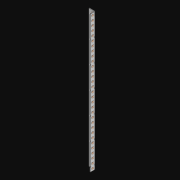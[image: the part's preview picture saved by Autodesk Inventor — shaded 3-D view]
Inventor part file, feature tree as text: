
AUTODESK INVENTOR PART (.ipt)
format: ipt  version: 2021 (Build 250183000, 183)  size: 1,305,600 bytes
history: native  units: in
note: dims shown in document units (in); Inventor stores cm internally (conversion verified against a paired STEP export)
features: extrude x64, other x62, sketch x4, pattern_linear x2, sheet_metal_op x1
ambient origin geometry x8: Origin, YZ Plane, XZ Plane, XY Plane, X Axis, Y Axis, Z Axis, Center Point
bodies: Solid1 (feature_tree)
feature tree (133):
  pattern_linear  "Rectangular Pattern1"  Spacing1=0.5in  [1 undecoded]
  pattern_linear  "Rectangular Pattern3"  Count1=31  [1 undecoded]
  extrude  "Extrusion1"  Depth=0.5in
  extrude  "Extrusion2"  Depth=0.5in
  sketch  "Sketch1"  dims[d0=0.182in]
  other  "Srf1"
  sketch  "Sketch3"  dims[d1=0.063in d2=0.0in]
  other  "Srf3"
  other  "Srf4"
  other  "Srf5"
  other  "Srf6"
  other  "Srf7"
  other  "Srf8"
  other  "Srf9"
  other  "Srf10"
  other  "Srf11"
  other  "Srf12"
  other  "Srf13"
  other  "Srf14"
  other  "Srf15"
  other  "Srf16"
  other  "Srf17"
  other  "Srf18"
  other  "Srf19"
  other  "Srf20"
  other  "Srf21"
  other  "Srf22"
  other  "Srf23"
  other  "Srf24"
  other  "Srf25"
  other  "Srf26"
  other  "Srf27"
  other  "Srf28"
  other  "Srf29"
  other  "Srf30"
  other  "Srf31"
  other  "Srf32"
  other  "Srf33"
  other  "Srf142"
  other  "Srf143"
  other  "Srf144"
  other  "Srf145"
  other  "Srf146"
  other  "Srf147"
  other  "Srf148"
  other  "Srf149"
  other  "Srf150"
  other  "Srf151"
  other  "Srf152"
  other  "Srf153"
  other  "Srf154"
  other  "Srf155"
  other  "Srf156"
  other  "Srf157"
  other  "Srf158"
  other  "Srf159"
  other  "Srf160"
  other  "Srf161"
  other  "Srf162"
  other  "Srf163"
  other  "Srf164"
  other  "Srf165"
  other  "Srf166"
  other  "Srf167"
  other  "Srf168"
  other  "Srf169"
  other  "Srf170"
  other  "Srf171"
  sketch  "Sketch4"  dims[d6=0.182in]
  sketch  "Sketch5"  dims[d7=0.063in d8=0.0in d11=0.5in d12=0.3937in d14=0.5in d18=12.2047in d20=0.5in d21=2.0in d22=0.0in d23=0.841in d24=0.0in]
  sheet_metal_op  "Fold1"
  extrude  "ExtrusionSrf1"  TaperAngle=0.0deg  [1 undecoded]
  extrude  "ExtrusionSrf3"  Depth=0.5in TaperAngle=0.0deg
  extrude  "ExtrusionSrf4"  [1 undecoded]
  extrude  "ExtrusionSrf5"  [1 undecoded]
  extrude  "ExtrusionSrf6"  [1 undecoded]
  extrude  "ExtrusionSrf7"  [1 undecoded]
  extrude  "ExtrusionSrf8"  [1 undecoded]
  extrude  "ExtrusionSrf9"  [1 undecoded]
  extrude  "ExtrusionSrf10"  [1 undecoded]
  extrude  "ExtrusionSrf11"  [1 undecoded]
  extrude  "ExtrusionSrf12"  [1 undecoded]
  extrude  "ExtrusionSrf13"  [1 undecoded]
  extrude  "ExtrusionSrf14"  [1 undecoded]
  extrude  "ExtrusionSrf15"  [1 undecoded]
  extrude  "ExtrusionSrf16"  [1 undecoded]
  extrude  "ExtrusionSrf17"  [1 undecoded]
  extrude  "ExtrusionSrf18"  [1 undecoded]
  extrude  "ExtrusionSrf19"  [1 undecoded]
  extrude  "ExtrusionSrf20"  [1 undecoded]
  extrude  "ExtrusionSrf21"  [1 undecoded]
  extrude  "ExtrusionSrf22"  [1 undecoded]
  extrude  "ExtrusionSrf23"  [1 undecoded]
  extrude  "ExtrusionSrf24"  [1 undecoded]
  extrude  "ExtrusionSrf25"  [1 undecoded]
  extrude  "ExtrusionSrf26"  [1 undecoded]
  extrude  "ExtrusionSrf27"  [1 undecoded]
  extrude  "ExtrusionSrf28"  [1 undecoded]
  extrude  "ExtrusionSrf29"  [1 undecoded]
  extrude  "ExtrusionSrf30"  [1 undecoded]
  extrude  "ExtrusionSrf31"  [1 undecoded]
  extrude  "ExtrusionSrf32"  [1 undecoded]
  extrude  "ExtrusionSrf33"  [1 undecoded]
  extrude  "ExtrusionSrf142"  [1 undecoded]
  extrude  "ExtrusionSrf143"  [1 undecoded]
  extrude  "ExtrusionSrf144"  [1 undecoded]
  extrude  "ExtrusionSrf145"  [1 undecoded]
  extrude  "ExtrusionSrf146"  [1 undecoded]
  extrude  "ExtrusionSrf147"  [1 undecoded]
  extrude  "ExtrusionSrf148"  [1 undecoded]
  extrude  "ExtrusionSrf149"  [1 undecoded]
  extrude  "ExtrusionSrf150"  [1 undecoded]
  extrude  "ExtrusionSrf151"  [1 undecoded]
  extrude  "ExtrusionSrf152"  [1 undecoded]
  extrude  "ExtrusionSrf153"  [1 undecoded]
  extrude  "ExtrusionSrf154"  [1 undecoded]
  extrude  "ExtrusionSrf155"  [1 undecoded]
  extrude  "ExtrusionSrf156"  [1 undecoded]
  extrude  "ExtrusionSrf157"  [1 undecoded]
  extrude  "ExtrusionSrf158"  [1 undecoded]
  extrude  "ExtrusionSrf159"  [1 undecoded]
  extrude  "ExtrusionSrf160"  [1 undecoded]
  extrude  "ExtrusionSrf161"  [1 undecoded]
  extrude  "ExtrusionSrf162"  [1 undecoded]
  extrude  "ExtrusionSrf163"  [1 undecoded]
  extrude  "ExtrusionSrf164"  [1 undecoded]
  extrude  "ExtrusionSrf165"  [1 undecoded]
  extrude  "ExtrusionSrf166"  [1 undecoded]
  extrude  "ExtrusionSrf167"  [1 undecoded]
  extrude  "ExtrusionSrf168"  [1 undecoded]
  extrude  "ExtrusionSrf169"  [1 undecoded]
  extrude  "ExtrusionSrf170"  [1 undecoded]
  extrude  "ExtrusionSrf171"  [1 undecoded]
note: 63 required parameter values undecoded (feature->parameter linkage not recoverable at this tier; creation-order binding heuristic only, values carry confidence <= 0.55)
